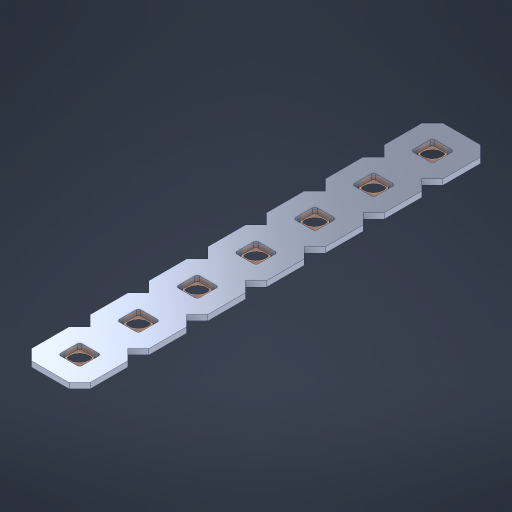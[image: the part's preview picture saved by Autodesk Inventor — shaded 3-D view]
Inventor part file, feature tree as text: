
AUTODESK INVENTOR PART (.ipt)
format: ipt  version: 2023 (Build 270158000, 158)  size: 349,696 bytes
history: native  units: in
note: dims shown in document units (in); Inventor stores cm internally (conversion verified against a paired STEP export)
features: other x8, extrude x6, sketch x2, pattern_linear x1
ambient origin geometry x8: Origin, YZ Plane, XZ Plane, XY Plane, X Axis, Y Axis, Z Axis, Center Point
bodies: Solid1 (feature_tree), Body (feature_tree)
feature tree (17):
  pattern_linear  "Rectangular Pattern1"  Spacing1=0.09in  [1 undecoded]
  sketch  "Sketch1"  dims[d1=0.5in]
  sketch  "Sketch2"  dims[d2=0.182in d3=0.09in d4=0.09in d5=0.09in d6=0.09in d7=0.09in d8=0.09in d9=0.09in d10=0.09in d11=0.02in d13=0.0in d14=0.172in d15=0.0625in d16=0.0in d19=0.5in d22=0.5in]
  other  "Srf1"
  other  "Srf126"
  other  "Srf127"
  other  "Srf128"
  other  "Srf129"
  other  "Srf130"
  other  "Srf131"
  other  "Circle"
  extrude  "ExtrusionSrf126"  Depth=0.09in
  extrude  "ExtrusionSrf127"  Depth=0.09in
  extrude  "ExtrusionSrf128"  Depth=0.09in
  extrude  "ExtrusionSrf129"  Depth=0.09in
  extrude  "ExtrusionSrf130"  Depth=0.09in
  extrude  "ExtrusionSrf131"  Depth=0.09in
note: 1 required parameter value undecoded (feature->parameter linkage not recoverable at this tier; creation-order binding heuristic only, values carry confidence <= 0.55)
